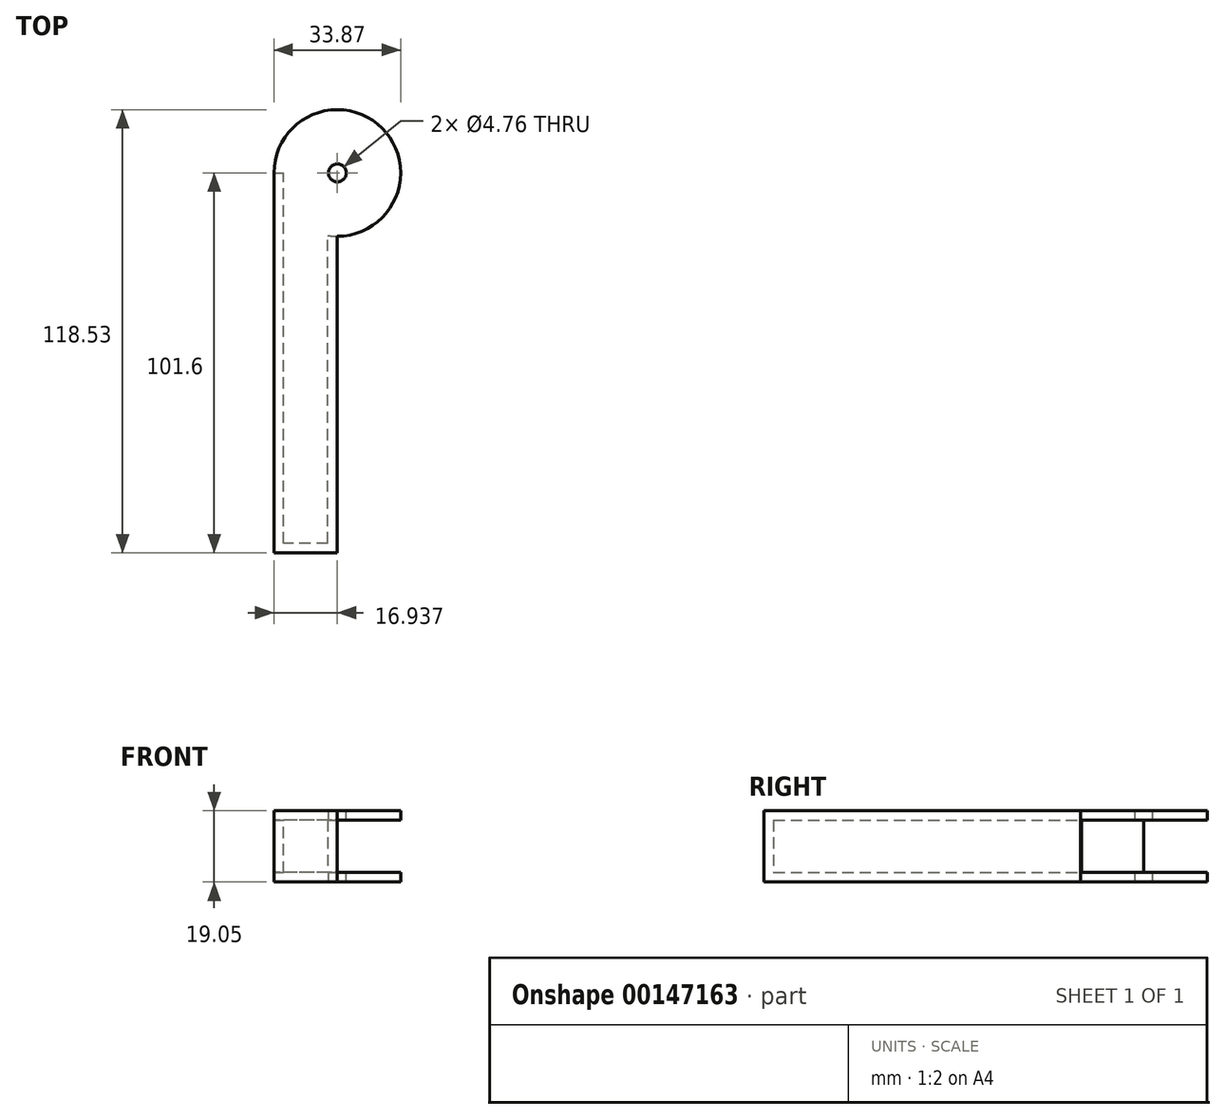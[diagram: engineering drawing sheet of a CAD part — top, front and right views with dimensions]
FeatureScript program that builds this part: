
annotation { "Feature Type Name" : "Feature", "Feature Type Description" : "" }
export const myFeature = defineFeature(function(context is Context, id is Id, definition is map)
    precondition{}
    {
        {
            var Q0;
            Q0=qCreatedBy(makeId("Top.planeOp"),FACE);
            var sketch = newSketch(context, id + "F0", { "sketchPlane" : qUnion([Q0])});
            skLineSegment(sketch, "E0.bottom", {"start": v(8.47, -50.8) * mm, "end": v(-8.47, -50.8) * mm});
            skLineSegment(sketch, "E0.left", {"start": v(8.47, -50.8) * mm, "end": v(8.47, 33.87) * mm});
            skLineSegment(sketch, "E0.right", {"start": v(-8.47, -50.8) * mm, "end": v(-8.47, 50.8) * mm});
            skPoint(sketch, "E0.middle", {"position": v(0, 0) * mm});
            skArc(sketch, "E1", {"start": v(8.47, 33.87) * mm, "mid": v(20.44, 62.77) * mm, "end": v(-8.47, 50.8) * mm});
            skSolve(sketch);
        }
        {
            var Q0;
            Q0=makeQuery(id+"F0.imprint","IMPRINT",FACE,{"disambiguationData":[TD([[makeQuery(id+"F0.imprint","IMPRINT",EDGE,{"derivedFrom":sQuery(id+"F0.wireOp",EDGE,"E0.bottom")}),-1.0]])]});
            extrude(context, id + "F1", {"entities" : qUnion([Q0]), "depth" : 19.05 * mm});
        }
        {
            var Q0;
            Q0=makeQuery(id+"F1.opExtrude","SWEPT_FACE",FACE,{"disambiguationData":[OSD([sQuery(id+"F0.wireOp",EDGE,"E1")])]});
            shell(context, id + "F2", {"entities" : qUnion([Q0]), "thickness" : 2.54 * mm});
        }
        {
            var Q0;
            Q0=makeQuery(id+"F1.opExtrude","CAP_FACE",FACE,{"disambiguationData":[OSD([sQuery(id+"F0.wireOp",EDGE,"E0.bottom"),sQuery(id+"F0.wireOp",EDGE,"E0.left"),sQuery(id+"F0.wireOp",EDGE,"E0.right"),sQuery(id+"F0.wireOp",EDGE,"E1")])],"isStart":false});
            var sketch = newSketch(context, id + "F3", { "sketchPlane" : qUnion([Q0])});
            skPoint(sketch, "E2", {"position": v(8.47, 50.8) * mm});
            skSolve(sketch);
        }
        {
            var Q0;
            Q0=sQuery(id+"F3.wireOp",VERTEX,"E2");
            var Q1;
            Q1=makeQuery(id+"F1.opExtrude","SWEPT_BODY",BODY,{"disambiguationData":[OSD([sQuery(id+"F0.wireOp",EDGE,"E0.bottom"),sQuery(id+"F0.wireOp",EDGE,"E0.left"),sQuery(id+"F0.wireOp",EDGE,"E0.right"),sQuery(id+"F0.wireOp",EDGE,"E1")])]});
            hole(context, id + "F4", {"style" : HoleStyle.SIMPLE, "endStyle" : HoleEndStyle.THROUGH, "holeDiameter" : 4.76 * mm, "locations" : qUnion([Q0]), "scope" : qUnion([Q1]), "isTappedThrough" : true});
        }
    });
